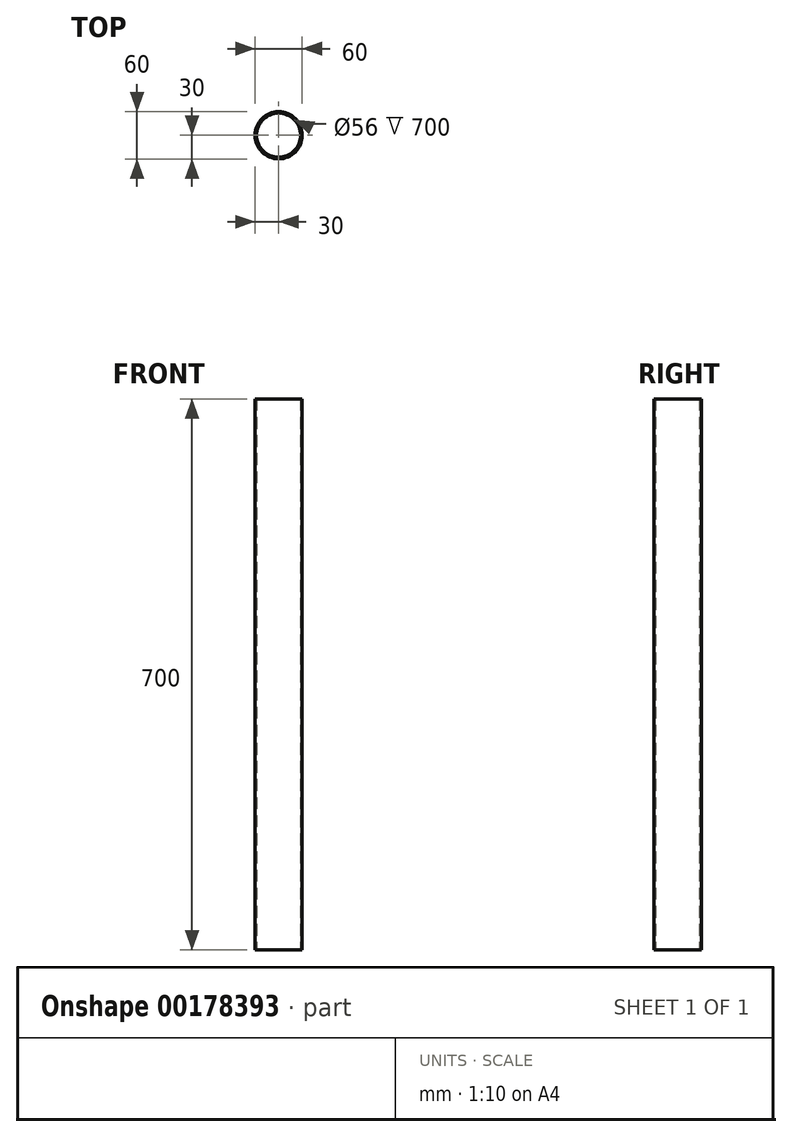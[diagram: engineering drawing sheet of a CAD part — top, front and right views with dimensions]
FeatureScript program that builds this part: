
annotation { "Feature Type Name" : "Feature", "Feature Type Description" : "" }
export const myFeature = defineFeature(function(context is Context, id is Id, definition is map)
    precondition{}
    {
        {
            var Q0;
            Q0=qCreatedBy(makeId("Top.planeOp"),FACE);
            var sketch = newSketch(context, id + "F0", { "sketchPlane" : qUnion([Q0])});
            skCircle(sketch, "E0", {"center": v(0, 0) * mm, "radius": 30 * mm});
            skCircle(sketch, "E1.0", {"center": v(0, 0) * mm, "radius": 28 * mm});
            skSolve(sketch);
        }
        {
            var Q0;
            Q0=makeQuery(id+"F0.imprint","IMPRINT",FACE,{"disambiguationData":[TD([[makeQuery(id+"F0.imprint","IMPRINT",EDGE,{"derivedFrom":sQuery(id+"F0.wireOp",EDGE,"E0")}),1.0]])]});
            extrude(context, id + "F1", {"entities" : qUnion([Q0]), "depth" : 700 * mm});
        }
    });
